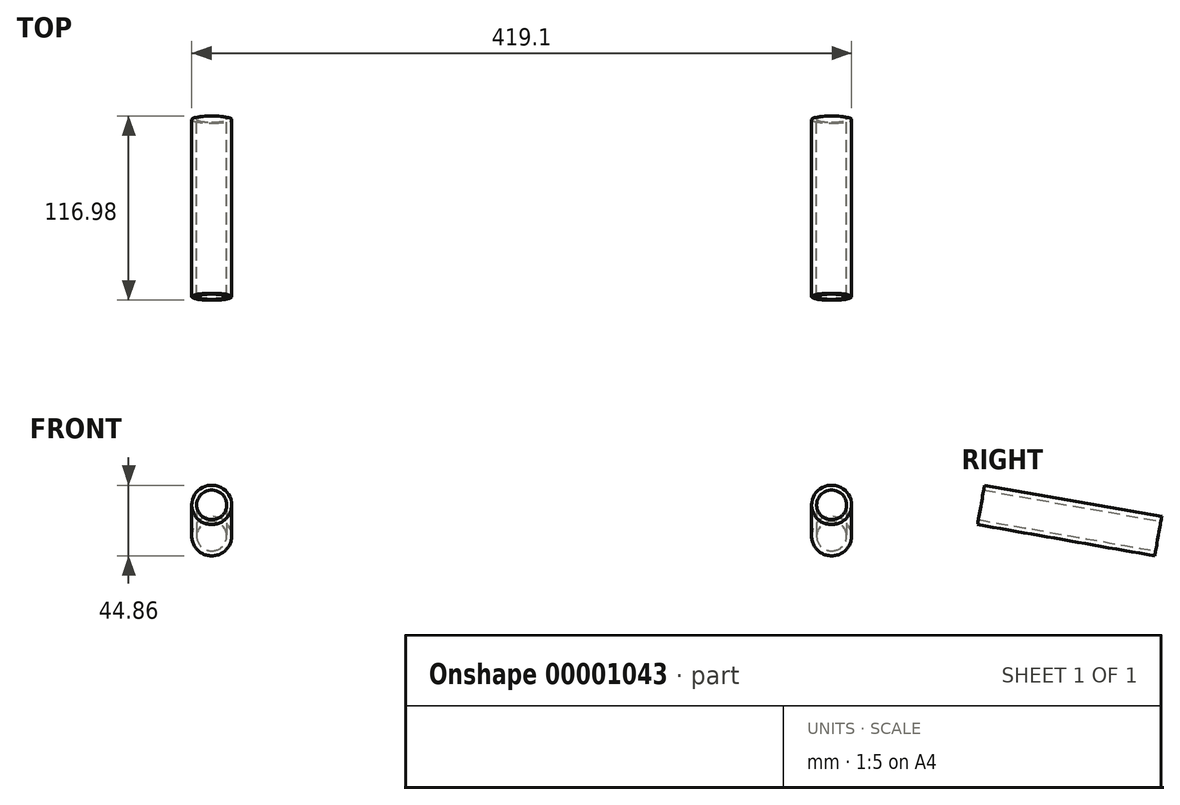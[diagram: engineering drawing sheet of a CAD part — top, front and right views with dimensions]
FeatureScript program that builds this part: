
annotation { "Feature Type Name" : "Feature", "Feature Type Description" : "" }
export const myFeature = defineFeature(function(context is Context, id is Id, definition is map)
    precondition{}
    {
        {
            var Q0;
            Q0=qCreatedBy(makeId("Right.planeOp"),FACE);
            var sketch = newSketch(context, id + "F0", { "sketchPlane" : qUnion([Q0])});
            skCircle(sketch, "E0", {"center": v(0, 0) * mm, "radius": 9.53 * mm});
            skSolve(sketch);
        }
        {
            var Q0;
            Q0=qCreatedBy(makeId("Right.planeOp"),FACE);
            var sketch = newSketch(context, id + "F1", { "sketchPlane" : qUnion([Q0])});
            skCircle(sketch, "E1", {"center": v(0, 0) * mm, "radius": 7.94 * mm});
            skSolve(sketch);
        }
        {
            var Q0;
            Q0=sQuery(id+"F0.wireOp",EDGE,"E0");
            var Q1;
            Q1=sQuery(id+"F1.wireOp",EDGE,"E1");
            extrude(context, id + "F2", {"bodyType" : ToolBodyType.SURFACE, "surfaceEntities" : qUnion([Q0, Q1]), "depth" : 368.3 * mm});
        }
        {
            var Q0;
            Q0=qCreatedBy(makeId("Front.planeOp"),FACE);
            var sketch = newSketch(context, id + "F3", { "sketchPlane" : qUnion([Q0])});
            skCircle(sketch, "E2", {"center": v(-12.7, 0) * mm, "radius": 12.7 * mm});
            skCircle(sketch, "E3", {"center": v(-12.7, 0) * mm, "radius": 9.53 * mm});
            skSolve(sketch);
        }
        {
            var Q0;
            Q0 = qSketchRegion(id + "F3", true);
            extrude(context, id + "F4", {"entities" : qUnion([Q0]), "depth" : 28.57 * mm, "hasSecondDirection" : true, "secondDirectionOppositeDirection" : true, "secondDirectionDepth" : 85.72 * mm});
        }
        {
            var Q0;
            Q0=makeQuery(id+"F4.opExtrude","SWEPT_BODY",BODY,{"disambiguationData":[OSD([sQuery(id+"F3.wireOp",EDGE,"E2"),sQuery(id+"F3.wireOp",EDGE,"E3")])]});
            var Q1;
            Q1=makeQuery(id+"F2.opExtrude","SWEPT_FACE",FACE,{"disambiguationData":[OSD([sQuery(id+"F0.wireOp",EDGE,"E0")])]});
            transform(context, id + "F5", {"entities" : qUnion([Q0]), "transformType" : TransformType.ROTATION, "transformAxis" : qUnion([Q1]), "angle" : 350 * degree, "makeCopy" : false});
        }
        {
            var Q0;
            Q0=makeQuery(id+"F4.opExtrude","SWEPT_BODY",BODY,{"disambiguationData":[OSD([sQuery(id+"F3.wireOp",EDGE,"E2"),sQuery(id+"F3.wireOp",EDGE,"E3")])]});
            transform(context, id + "F6", {"entities" : qUnion([Q0]), "transformType" : TransformType.TRANSLATION_3D, "dx" : 393.7 * mm, "dy" : 0 * mm, "dz" : 0 * mm, "makeCopy" : true});
        }
        {
            var Q0;
            Q0=qCreatedBy(makeId("Front.planeOp"),FACE);
            cPlane(context, id + "F7", {"entities" : qUnion([Q0]), "cplaneType" : CPlaneType.OFFSET, "offset" : 9.52 * mm, "width" : 152.4 * mm, "height" : 152.4 * mm});
        }
        {
            var Q0;
            Q0=qCreatedBy(makeId("Top.planeOp"),FACE);
            var sketch = newSketch(context, id + "F8", { "sketchPlane" : qUnion([Q0])});
            skCircle(sketch, "E4", {"center": v(9.53, -9.49) * mm, "radius": 9.53 * mm});
            skCircle(sketch, "E5", {"center": v(9.53, -9.49) * mm, "radius": 7.94 * mm});
            skSolve(sketch);
        }
        {
            var Q0;
            Q0=sQuery(id+"F8.wireOp",EDGE,"E4");
            var Q1;
            Q1=sQuery(id+"F8.wireOp",EDGE,"E5");
            extrude(context, id + "F9", {"bodyType" : ToolBodyType.SURFACE, "surfaceEntities" : qUnion([Q0, Q1]), "oppositeDirection" : true, "depth" : 517.52 * mm, "hasSecondDirection" : true, "secondDirectionOppositeDirection" : false, "secondDirectionDepth" : 279.4 * mm});
        }
        {
            var Q0;
            Q0=makeQuery(id+"F9.opExtrude","SWEPT_BODY",BODY,{"disambiguationData":[OSD([sQuery(id+"F8.wireOp",EDGE,"E4")])]});
            var Q1;
            Q1=makeQuery(id+"F9.opExtrude","SWEPT_BODY",BODY,{"disambiguationData":[OSD([sQuery(id+"F8.wireOp",EDGE,"E5")])]});
            transform(context, id + "F10", {"entities" : qUnion([Q0, Q1]), "transformType" : TransformType.TRANSLATION_3D, "dx" : 0 * mm, "dy" : -9.52 * mm, "dz" : 0 * mm, "makeCopy" : false});
        }
        {
            var Q0;
            Q0=makeQuery(id+"F9.opExtrude","SWEPT_BODY",BODY,{"disambiguationData":[OSD([sQuery(id+"F8.wireOp",EDGE,"E4")])]});
            var Q1;
            Q1=makeQuery(id+"F9.opExtrude","SWEPT_BODY",BODY,{"disambiguationData":[OSD([sQuery(id+"F8.wireOp",EDGE,"E5")])]});
            var Q2;
            Q2=makeQuery(id+"F2.opExtrude","SWEPT_FACE",FACE,{"disambiguationData":[OSD([sQuery(id+"F0.wireOp",EDGE,"E0")])]});
            transform(context, id + "F11", {"entities" : qUnion([Q0, Q1]), "transformType" : TransformType.TRANSLATION_DISTANCE, "transformDirection" : qUnion([Q2]), "distance" : 349.25 * mm, "makeCopy" : true});
        }
    });
